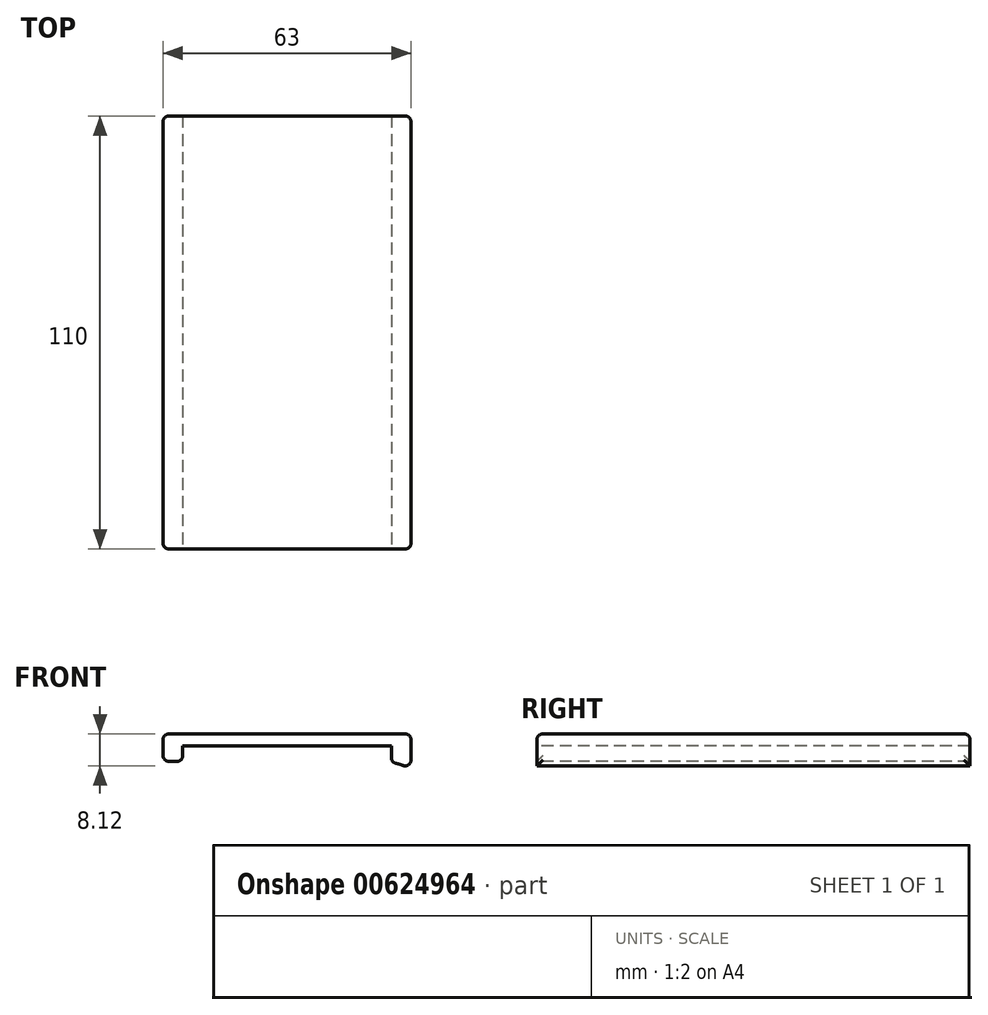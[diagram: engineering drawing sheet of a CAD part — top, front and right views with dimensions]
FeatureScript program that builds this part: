
annotation { "Feature Type Name" : "Feature", "Feature Type Description" : "" }
export const myFeature = defineFeature(function(context is Context, id is Id, definition is map)
    precondition{}
    {
        {
            var Q0;
            Q0=qCreatedBy(makeId("Front.planeOp"),FACE);
            var sketch = newSketch(context, id + "F0", { "sketchPlane" : qUnion([Q0])});
            skLineSegment(sketch, "E0.bottom", {"start": v(31.5, 3) * mm, "end": v(-31.5, 3) * mm});
            skLineSegment(sketch, "E0.left", {"start": v(31.5, 3) * mm, "end": v(31.5, -6) * mm});
            skLineSegment(sketch, "E0.right", {"start": v(-31.5, 3) * mm, "end": v(-31.5, -4) * mm});
            skPoint(sketch, "E0.middle", {"position": v(0, 0) * mm});
            skLineSegment(sketch, "E1", {"start": v(26.5, 0) * mm, "end": v(-26.5, 0) * mm});
            skLineSegment(sketch, "E2", {"start": v(-26.5, 0) * mm, "end": v(-26.5, -4) * mm});
            skLineSegment(sketch, "E3", {"start": v(-26.5, -4) * mm, "end": v(-31.5, -4) * mm});
            skLineSegment(sketch, "E4", {"start": v(26.5, -4.5) * mm, "end": v(26.5, 0) * mm});
            skLineSegment(sketch, "E5", {"start": v(31.5, 0) * mm, "end": v(26.5, 0) * mm, "construction": true});
            skFitSpline(sketch, "E6", {"points": [v(31.5, -6) * mm, v(26.5, -4.5) * mm], "startDerivative": vector(-3.91, 1.58) * mm, "endDerivative": vector(-6.02, -0.96) * mm});
            skSolve(sketch);
        }
        {
            var Q0;
            Q0=makeQuery(id+"F0.imprint","IMPRINT",FACE,{"disambiguationData":[TD([[makeQuery(id+"F0.imprint","IMPRINT",EDGE,{"derivedFrom":sQuery(id+"F0.wireOp",EDGE,"E0.bottom")}),1.0]])]});
            extrude(context, id + "F1", {"entities" : qUnion([Q0]), "oppositeDirection" : true, "depth" : 110 * mm, "offsetDistance" : 25 * mm});
        }
        {
            var Q0;
            Q0=makeQuery(id+"F1.opExtrude","CAP_EDGE",EDGE,{"disambiguationData":[OSD([sQuery(id+"F0.wireOp",EDGE,"E0.bottom")])],"isStart":true});
            var Q1;
            Q1=makeQuery(id+"F1.opExtrude","SWEPT_EDGE",EDGE,{"disambiguationData":[OSD([sQuery(id+"F0.wireOp",EDGE,"E0.bottom"),sQuery(id+"F0.wireOp",EDGE,"E0.left")])]});
            var Q2;
            Q2=makeQuery(id+"F1.opExtrude","SWEPT_EDGE",EDGE,{"disambiguationData":[OSD([sQuery(id+"F0.wireOp",EDGE,"E0.bottom"),sQuery(id+"F0.wireOp",EDGE,"E0.right")])]});
            var Q3;
            Q3=makeQuery(id+"F1.opExtrude","CAP_EDGE",EDGE,{"disambiguationData":[OSD([sQuery(id+"F0.wireOp",EDGE,"E0.bottom")])],"isStart":false});
            var Q4;
            Q4=makeQuery(id+"F1.opExtrude","SWEPT_EDGE",EDGE,{"disambiguationData":[OSD([sQuery(id+"F0.wireOp",EDGE,"E0.right"),sQuery(id+"F0.wireOp",EDGE,"E3")])]});
            var Q5;
            Q5=makeQuery(id+"F1.opExtrude","SWEPT_EDGE",EDGE,{"disambiguationData":[OSD([sQuery(id+"F0.wireOp",EDGE,"E2"),sQuery(id+"F0.wireOp",EDGE,"E3")])]});
            var Q6;
            Q6=makeQuery(id+"F1.opExtrude","SWEPT_EDGE",EDGE,{"disambiguationData":[OSD([sQuery(id+"F0.wireOp",EDGE,"E4"),sQuery(id+"F0.wireOp",EDGE,"E6")])]});
            var Q7;
            Q7=makeQuery(id+"F1.opExtrude","SWEPT_EDGE",EDGE,{"disambiguationData":[OSD([sQuery(id+"F0.wireOp",EDGE,"E0.left"),sQuery(id+"F0.wireOp",EDGE,"E6")])]});
            var Q8;
            Q8=makeQuery(id+"F1.opExtrude","CAP_EDGE",EDGE,{"disambiguationData":[OSD([sQuery(id+"F0.wireOp",EDGE,"E0.right")])],"isStart":false});
            var Q9;
            Q9=makeQuery(id+"F1.opExtrude","CAP_EDGE",EDGE,{"disambiguationData":[OSD([sQuery(id+"F0.wireOp",EDGE,"E0.left")])],"isStart":false});
            var Q10;
            Q10=makeQuery(id+"F1.opExtrude","CAP_EDGE",EDGE,{"disambiguationData":[OSD([sQuery(id+"F0.wireOp",EDGE,"E0.right")])],"isStart":true});
            var Q11;
            Q11=makeQuery(id+"F1.opExtrude","CAP_EDGE",EDGE,{"disambiguationData":[OSD([sQuery(id+"F0.wireOp",EDGE,"E0.left")])],"isStart":true});
            fillet(context, id + "F2", {"entities" : qUnion([Q0, Q1, Q2, Q3, Q4, Q5, Q6, Q7, Q8, Q9, Q10, Q11]), "radius" : 1.5 * mm, "tangentPropagation" : true, "allowEdgeOverflow" : false});
        }
    });
